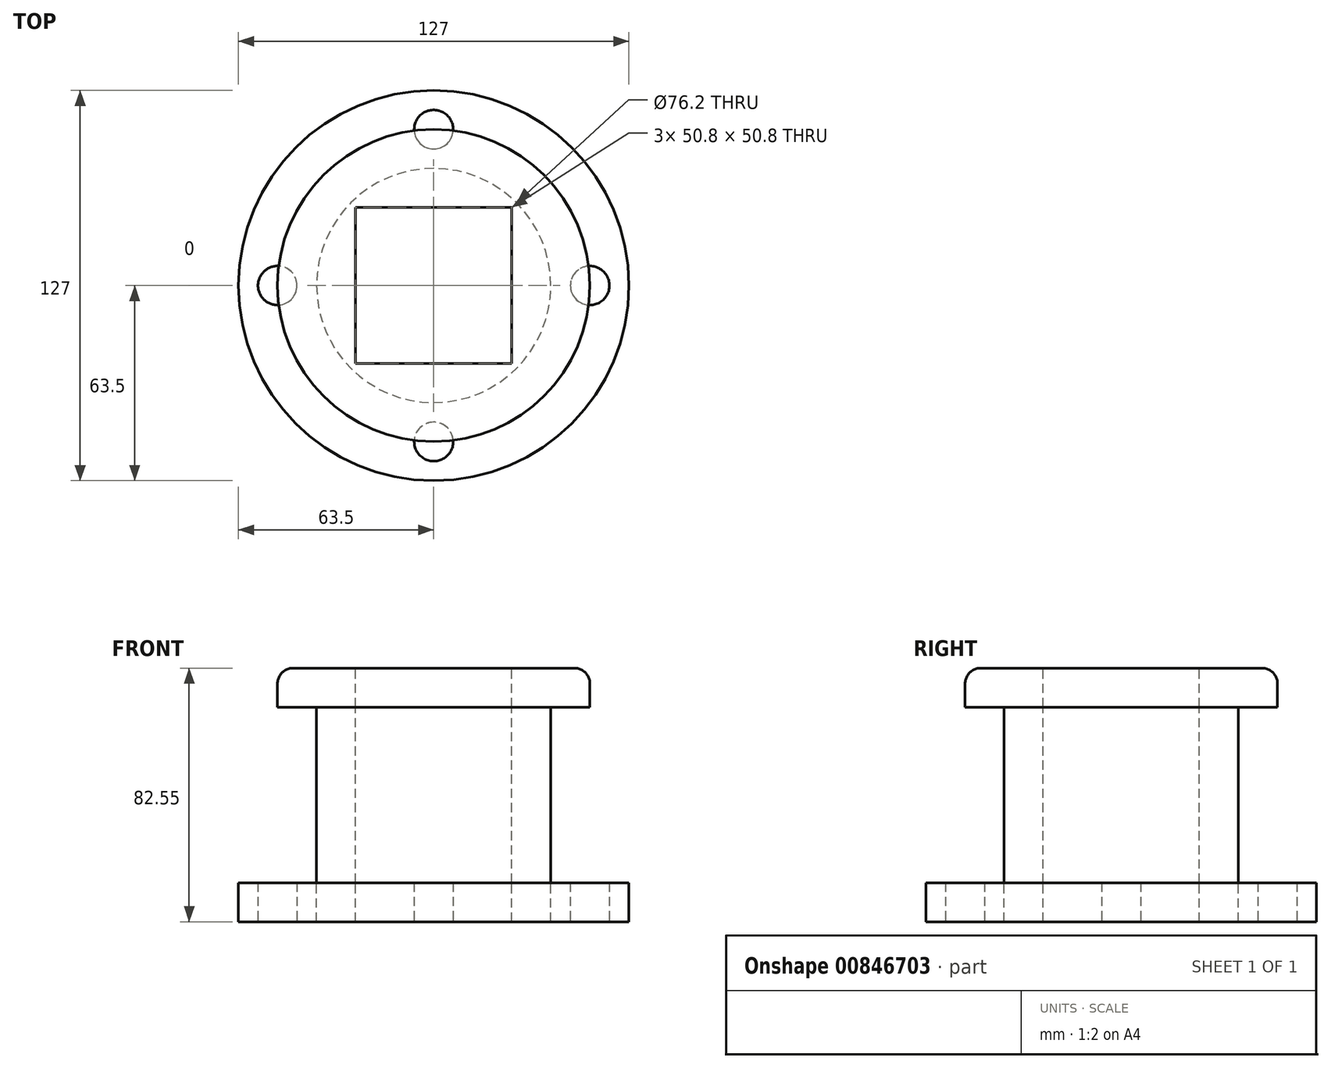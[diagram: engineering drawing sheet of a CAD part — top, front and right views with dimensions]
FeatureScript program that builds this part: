
annotation { "Feature Type Name" : "Feature", "Feature Type Description" : "" }
export const myFeature = defineFeature(function(context is Context, id is Id, definition is map)
    precondition{}
    {
        {
            var Q0;
            Q0=qCreatedBy(makeId("Top.planeOp"),FACE);
            var sketch = newSketch(context, id + "F0", { "sketchPlane" : qUnion([Q0])});
            skCircle(sketch, "E0", {"center": v(0, 0) * mm, "radius": 38.1 * mm});
            skCircle(sketch, "E1", {"center": v(0, 0) * mm, "radius": 50.8 * mm});
            skSolve(sketch);
        }
        {
            var Q0;
            Q0=makeQuery(id+"F0.imprint","IMPRINT",FACE,{"disambiguationData":[TD([[makeQuery(id+"F0.imprint","IMPRINT",EDGE,{"derivedFrom":sQuery(id+"F0.wireOp",EDGE,"E0")}),1.0]])]});
            extrude(context, id + "F1", {"entities" : qUnion([Q0]), "depth" : 57.15 * mm, "offsetDistance" : 25.4 * mm});
        }
        {
            var Q0;
            Q0=makeQuery(id+"F1.opExtrude","CAP_FACE",FACE,{"disambiguationData":[OSD([sQuery(id+"F0.wireOp",EDGE,"E0")])],"isStart":false});
            var sketch = newSketch(context, id + "F2", { "sketchPlane" : qUnion([Q0])});
            skCircle(sketch, "E2", {"center": v(0, 0) * mm, "radius": 50.8 * mm});
            skCircle(sketch, "E3", {"center": v(0, 0) * mm, "radius": 38.1 * mm});
            skSolve(sketch);
        }
        {
            var Q0;
            Q0=makeQuery(id+"F2.imprint","IMPRINT",FACE,{"disambiguationData":[TD([[makeQuery(id+"F2.imprint","IMPRINT",EDGE,{"derivedFrom":sQuery(id+"F2.wireOp",EDGE,"E2")}),1.0]])]});
            var Q1;
            Q1=makeQuery(id+"F2.imprint","IMPRINT",FACE,{"disambiguationData":[TD([[makeQuery(id+"F2.imprint","IMPRINT",EDGE,{"derivedFrom":sQuery(id+"F2.wireOp",EDGE,"E3")}),1.0]])]});
            extrude(context, id + "F3", {"entities" : qUnion([Q0, Q1]), "depth" : 12.7 * mm, "offsetDistance" : 25.4 * mm});
        }
        {
            var Q0;
            Q0=makeQuery(id+"F3.opExtrude","CAP_FACE",FACE,{"disambiguationData":[OSD([sQuery(id+"F2.wireOp",EDGE,"E2")])],"isStart":false});
            var sketch = newSketch(context, id + "F4", { "sketchPlane" : qUnion([Q0])});
            skLineSegment(sketch, "E4.bottom", {"start": v(-25.4, 25.4) * mm, "end": v(25.4, 25.4) * mm});
            skLineSegment(sketch, "E4.top", {"start": v(-25.4, -25.4) * mm, "end": v(25.4, -25.4) * mm});
            skLineSegment(sketch, "E4.left", {"start": v(-25.4, 25.4) * mm, "end": v(-25.4, -25.4) * mm});
            skLineSegment(sketch, "E4.right", {"start": v(25.4, 25.4) * mm, "end": v(25.4, -25.4) * mm});
            skPoint(sketch, "E4.middle", {"position": v(0, 0) * mm});
            skSolve(sketch);
        }
        {
            var Q0;
            Q0=makeQuery(id+"F4.imprint","IMPRINT",FACE,{"disambiguationData":[TD([[makeQuery(id+"F4.imprint","IMPRINT",EDGE,{"derivedFrom":sQuery(id+"F4.wireOp",EDGE,"E4.bottom")}),-1.0]])]});
            extrude(context, id + "F5", {"entities" : qUnion([Q0]), "operationType" : NewBodyOperationType.REMOVE, "oppositeDirection" : true, "depth" : 114.8 * mm, "offsetDistance" : 25.4 * mm});
        }
        {
            var Q0;
            Q0=makeQuery(id+"F1.opExtrude","CAP_FACE",FACE,{"disambiguationData":[OSD([sQuery(id+"F0.wireOp",EDGE,"E0")])],"isStart":true});
            var sketch = newSketch(context, id + "F6", { "sketchPlane" : qUnion([Q0])});
            skLineSegment(sketch, "E5.bottom", {"start": v(-25.4, 25.4) * mm, "end": v(25.4, 25.4) * mm});
            skLineSegment(sketch, "E5.top", {"start": v(-25.4, -25.4) * mm, "end": v(25.4, -25.4) * mm});
            skLineSegment(sketch, "E5.left", {"start": v(-25.4, 25.4) * mm, "end": v(-25.4, -25.4) * mm});
            skLineSegment(sketch, "E5.right", {"start": v(25.4, 25.4) * mm, "end": v(25.4, -25.4) * mm});
            skPoint(sketch, "E5.middle", {"position": v(0, 0) * mm});
            skSolve(sketch);
        }
        {
            var Q0;
            Q0=makeQuery(id+"F6.imprint","IMPRINT",FACE,{"disambiguationData":[TD([[makeQuery(id+"F6.imprint","IMPRINT",EDGE,{"derivedFrom":sQuery(id+"F6.wireOp",EDGE,"E5.bottom")}),-1.0]])]});
            extrude(context, id + "F7", {"entities" : qUnion([Q0]), "operationType" : NewBodyOperationType.REMOVE, "oppositeDirection" : true, "depth" : 73.4 * mm, "offsetDistance" : 25.4 * mm});
        }
        {
            var Q0;
            Q0=makeQuery(id+"F3.opExtrude","CAP_EDGE",EDGE,{"disambiguationData":[OSD([sQuery(id+"F2.wireOp",EDGE,"E2")])],"isStart":false});
            fillet(context, id + "F8", {"entities" : qUnion([Q0]), "radius" : 5.08 * mm, "tangentPropagation" : true, "allowEdgeOverflow" : false});
        }
        {
            var Q0;
            Q0=makeQuery(id+"F1.opExtrude","CAP_FACE",FACE,{"disambiguationData":[OSD([sQuery(id+"F0.wireOp",EDGE,"E0")])],"isStart":true});
            var sketch = newSketch(context, id + "F9", { "sketchPlane" : qUnion([Q0])});
            skCircle(sketch, "E6", {"center": v(0, 0) * mm, "radius": 63.5 * mm});
            skSolve(sketch);
        }
        {
            var Q0;
            Q0=makeQuery(id+"F9.imprint","IMPRINT",FACE,{"disambiguationData":[TD([[makeQuery(id+"F9.imprint","IMPRINT",EDGE,{"derivedFrom":sQuery(id+"F9.wireOp",EDGE,"E6")}),1.0]])]});
            extrude(context, id + "F10", {"entities" : qUnion([Q0]), "depth" : 12.7 * mm, "offsetDistance" : 25.4 * mm});
        }
        {
            var Q0;
            Q0=makeQuery(id+"F1.opExtrude","CAP_FACE",FACE,{"disambiguationData":[OSD([sQuery(id+"F0.wireOp",EDGE,"E0")])],"isStart":true});
            var sketch = newSketch(context, id + "F11", { "sketchPlane" : qUnion([Q0])});
            skCircle(sketch, "E7", {"center": v(0, 0) * mm, "radius": 38.1 * mm});
            skSolve(sketch);
        }
        {
            var Q0;
            Q0=makeQuery(id+"F11.imprint","IMPRINT",FACE,{"disambiguationData":[TD([[makeQuery(id+"F11.imprint","IMPRINT",EDGE,{"derivedFrom":sQuery(id+"F11.wireOp",EDGE,"E7")}),-1.0]])]});
            extrude(context, id + "F12", {"entities" : qUnion([Q0]), "depth" : 12.7 * mm, "offsetDistance" : 25.4 * mm});
        }
        {
            var Q0;
            Q0=makeQuery(id+"F10.opExtrude","CAP_FACE",FACE,{"disambiguationData":[OSD([sQuery(id+"F0.wireOp",EDGE,"E0"),sQuery(id+"F9.wireOp",EDGE,"E6")])],"isStart":false});
            var sketch = newSketch(context, id + "F13", { "sketchPlane" : qUnion([Q0])});
            skCircle(sketch, "E8", {"center": v(0, 50.8) * mm, "radius": 6.35 * mm});
            skCircle(sketch, "E9", {"center": v(50.8, 0) * mm, "radius": 6.35 * mm});
            skCircle(sketch, "E10", {"center": v(0, -50.8) * mm, "radius": 6.35 * mm});
            skCircle(sketch, "E11", {"center": v(-50.8, 0) * mm, "radius": 6.35 * mm});
            skSolve(sketch);
        }
        {
            var Q0;
            Q0=makeQuery(id+"F13.imprint","IMPRINT",FACE,{"disambiguationData":[TD([[makeQuery(id+"F13.imprint","IMPRINT",EDGE,{"derivedFrom":sQuery(id+"F13.wireOp",EDGE,"E8")}),1.0]])]});
            var Q1;
            Q1=makeQuery(id+"F13.imprint","IMPRINT",FACE,{"disambiguationData":[TD([[makeQuery(id+"F13.imprint","IMPRINT",EDGE,{"derivedFrom":sQuery(id+"F13.wireOp",EDGE,"E11")}),1.0]])]});
            var Q2;
            Q2=makeQuery(id+"F13.imprint","IMPRINT",FACE,{"disambiguationData":[TD([[makeQuery(id+"F13.imprint","IMPRINT",EDGE,{"derivedFrom":sQuery(id+"F13.wireOp",EDGE,"E10")}),1.0]])]});
            var Q3;
            Q3=makeQuery(id+"F13.imprint","IMPRINT",FACE,{"disambiguationData":[TD([[makeQuery(id+"F13.imprint","IMPRINT",EDGE,{"derivedFrom":sQuery(id+"F13.wireOp",EDGE,"E9")}),1.0]])]});
            extrude(context, id + "F14", {"entities" : qUnion([Q0, Q1, Q2, Q3]), "operationType" : NewBodyOperationType.REMOVE, "oppositeDirection" : true, "depth" : 25.4 * mm, "offsetDistance" : 25.4 * mm});
        }
    });
